# Revit family: Drinking_Fountain-Haws_Corporation-Pedestal_3600
name_source: partatom
category: Plumbing Fixtures
revit_build: Autodesk Revit 2015 (Build: 20140606_1530(x64)
units: mm (PartAtom-declared; Revit-internal decimal feet)

## types (4) — shared parameters
BIMobject category = Taps & Mixers
BIMobject category code = sanitary-taps-mixers
BIMobject main category = Sanitary
BIMobject main category code = sanitary
Brand url = https://www.hawsco.com
Default Elevation = 48"
Design country = United States
Edition number = 1
Installation instructions = https://www.hawsco.com
Manufacturer = Haws Corporation
Manufacturer country = United States
Manufacturer name = Haws Corporation
Masterformat 2014 Code = 22 47 13
Masterformat 2014 Description = Drinking Fountains
Material main = Metal
Material_chrome = Metal - Haws Corporation - Polished Chrome - 5703M
Material_inserts = Acetal Resin-Haws Corporation- Black
Nominal height = 43"
Nominal width = 28"
OmniClass Code = 23-31 31 00
OmniClass Description = Drinking Fountains
Pedestal = Metal - Haws Corporation - Green Powder Coated Finish
Product Guid = 4b9aadb5-b5f9-4fd1-bd63-5e5384db43e9
Product SKU = haws-3602
Product data url = https://bimobject.com
Product family = Drinking Fountains/Coolers
Product group = Pedestal Mounted Drinking Fountains
Product url = https://www.hawsco.com
QR code = http://bimobject.com
Technical description = https://www.hawsco.com
URL = www.hawsco.com/
Uniclass 1.4 Code = L7213
Uniclass 1.4 Description = Fountains
Uniclass 2.0 Code = SS-35-65-70-25
Uniclass 2.0 Description = Drinking Fountain Systems
Uniclass 2015 Code = Pr_40_20_87_24
Uniclass 2015 Name = Drinking fountains
Weight Net (Kg) = 0

## per-type parameters (varying)
| type | 3602 | 3602-3611-3612 | 3610 | 3610-3611-3612 | 3611 | 3612 | Description | Flow Rate | Model |
| IN3602 | Yes | Yes | No | No | No | No | Modular Outdoor Drinking Fountain | 0.0 GPM | 3602 |
| IN3610 | No | No | Yes | Yes | No | No | Modular Outdoor Bottle Filler | 1.0 GPM | 3610 |
| IN3611 | No | Yes | No | Yes | Yes | No | Modular Outdoor Bottle Filler and Drinking Fountain | 1.0 GPM | 3611 |
| IN3612 | No | Yes | No | Yes | No | Yes | Modular Outdoor Bottle Filler and Double Drinking Fountain | 1.0 GPM | 3612 |

## geometry (parser evidence)
native form markers: Blend x4, Sweep x12
no freeform markers — native parametric forms only
